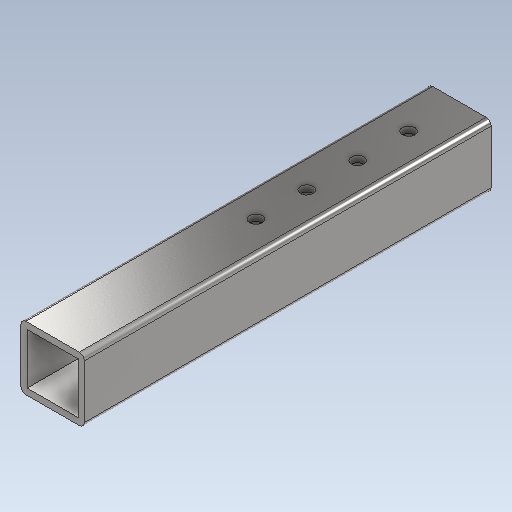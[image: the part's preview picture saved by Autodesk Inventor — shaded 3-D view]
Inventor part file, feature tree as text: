
AUTODESK INVENTOR PART (.ipt)
format: ipt  version: 2021 (Build 250183000, 183)  size: 222,720 bytes
history: native  units: mm
features: plane x2, split x2, sketch x2, extrude x1, fillet x1, hole x1, pattern_linear x1
ambient origin geometry x8: Origin, YZ Plane, XZ Plane, XY Plane, X Axis, Y Axis, Z Axis, Center Point
bodies: Solid1 (feature_tree), Solid2 (feature_tree), Solid3 (feature_tree)
feature tree (10):
  extrude  "Extrusion1"  Depth=25.0mm
  fillet  "Fillet1"  Radius=12.5mm
  plane  "Work Plane1"
  split  "Split1"
  hole  "Hole1"  [1 undecoded]
  pattern_linear  "Rectangular Pattern1"  Count1=100 Spacing1=0.0mm
  plane  "Work Plane3"
  split  "Split3"
  sketch  "Sketch1"  dims[d0=25.0mm d1=25.0mm d2=12.5mm]
  sketch  "Sketch2"  dims[d3=12.5mm d4=2.5mm d5=1000.0mm d6=0.0mm d7=2.0mm d8=-160.0mm d9=0.0mm d10=20.0mm d11=5.0mm d12=6.0mm d13=4.0mm d14=2.0mm d15=90.0deg d16=8.0mm d17=20.594885mm d18=40.0mm d20=20.0mm d22=-24.5mm]
note: 1 required parameter value undecoded (feature->parameter linkage not recoverable at this tier; creation-order binding heuristic only, values carry confidence <= 0.55)
